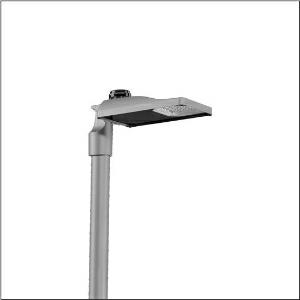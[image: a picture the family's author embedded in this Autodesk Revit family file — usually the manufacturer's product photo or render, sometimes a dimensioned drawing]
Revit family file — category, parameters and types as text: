
# Revit family: streetlight_sl_31_micro___p1_0a_5xh5a75n08ca_0299
name_source: partatom
category: Lighting Fixtures
units: mm (PartAtom-declared; Revit-internal decimal feet)

## family parameters
Cut with Voids When Loaded = No
Host = Face
Light Source = No
Part Type = Normal
Room Calculation Point = No
Round Connector Dimension = Use Diameter
Shared = No

## types (1)
- --- (1 x LED, 1080 lm, 10.3 W, 2200K)
    Apparent Load = 10 VA
    CIE Flux Codes = 23 55 94 100 100
    Color Rendering = 70
    Color Temperature = 2200K
    Default Elevation = 1800 mm
    Description = Streetlight SL 31 micro NEMA (7pin), Desk-Remote mast luminaire for post-top, side-entry; light control with lens of PMMA; light distribution: P1.0a, direct asymmetric distribution, for standard-compliant lighting for roads and squares; LED: luminous flux: 1.080lm, light colour: 722, colour temperature: 2200K; luminous efficacy: 104,9lm/W; control: pre-setting: linear dimming characteristic, flexible luminous flux parameterisation, time-dependent luminous flux control, constant luminous flux control, intelligent temperature release in ECG and LED module, overheat protection; luminaire housing, of diecast aluminium, SITECO metallic grey (DB 702S), corrosivity category C5 high according to DIN EN ISO 12944; cover of toughened safety glass, transparent, opened without tools; mast flange of diecast aluminium, SITECO metallic grey (DB 702S), spigot size: 76/60mm, mast flange included unmounted; cable length: 5,5m, connection cable pre-assembled; mains connection: 220..240V, AC, 50/60Hz; power consumption (at start of service life): 10,3W / (at end of service life): 10,6W / (with reduced operation 50%): 5,3W; protection rating (complete): IP66; insulation class (complete): insulation class I (protective earthing); impact resistance: IK10; certification: CE, ENEC, ENEC+, VDE, UKCA; permissible operating ambient temperature for outdoor applications: -40..+50°C; packaging unit: 1 piece

Light Distribution: P1.0a
    Height = 76 mm
    Lamp = 1 x LED
    Lamp Light Flux = 1080 lm
    Lamp Power = 10.3 W
    Lamp count = 1
    Length = 467 mm
    Luminous efficacy = 105 lm/W
    Manufacturer = Siteco
    ModVariant = No
    Model = 5XH5A75N08CA
    Number of Poles = 1
    OnlyDefault = Yes
    Power Factor = 1
    Product Name = Streetlight SL 31 micro | P1.0a
    Product group = mast luminaire | pylon top
    ProductGroupID = 6100
    Protection Class = Protection class I
    Protection Degree = IP 66
    RLX_Detail_Level = 1
    RLX_Emergency_Light_Flux = 0 lm
    RLX_Emergency_Type = 0
    RLX_Emergency_Type_DB = No
    RlxData = <blob elided: 22621 chars, md5=ca386830>
    Socket = socket
    Standby Power = 0 W
    System Light Flux = 1080 lm
    System Power = 10 W
    Type Comments = factory setting: luminous flux: 100 % | dim-lin: 254 | 386 mA
    Type Image = l_1300305.jpg
    URL = http://relux.com
    VarID = @adj_008977
    Voltage = 0 V
    Weight = 0.00 kg
    Width = 265 mm

## geometry (parser evidence)
native form markers: Blend x4, Sweep x10
no freeform markers — native parametric forms only
